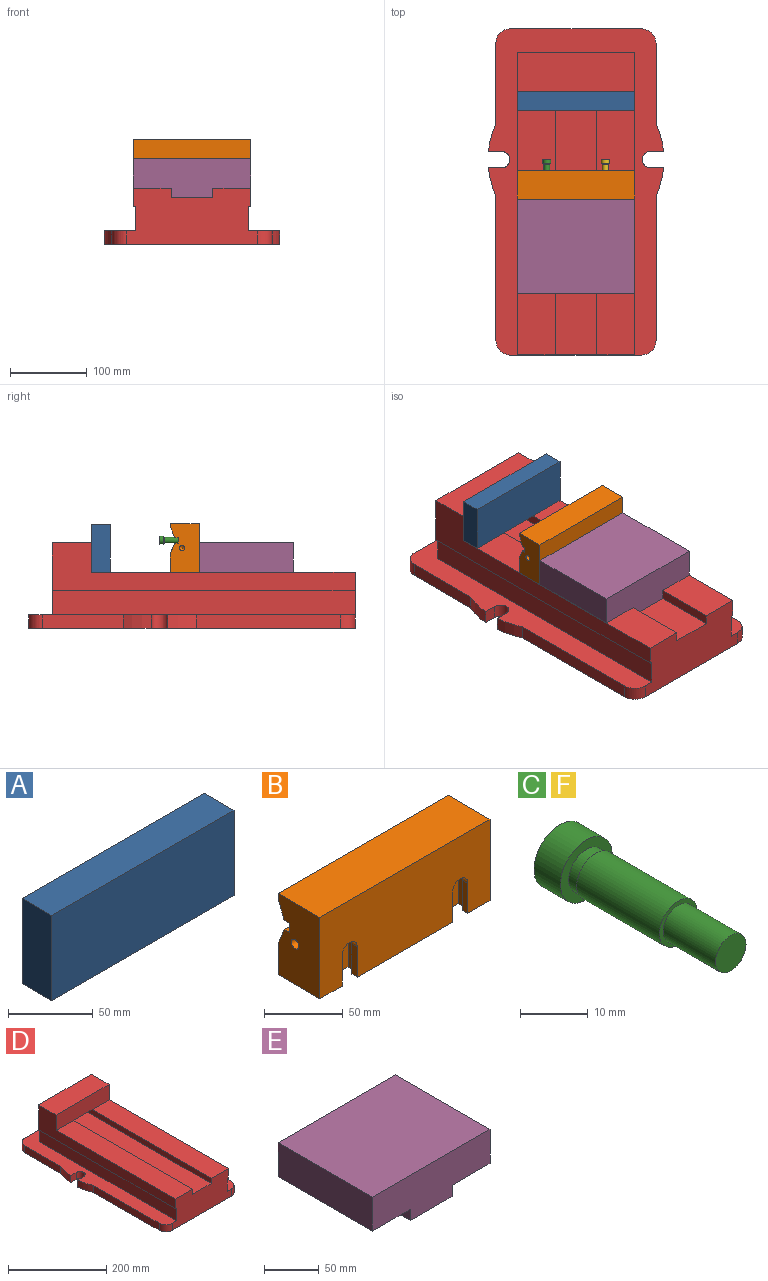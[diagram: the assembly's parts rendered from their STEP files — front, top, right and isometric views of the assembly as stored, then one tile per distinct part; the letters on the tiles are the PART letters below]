
ASSEMBLY  parts=6 mates=6
PART A: 6 faces, bbox 152.4x25x61.7 mm
  f0: plane 61.72x25.02mm, normal (-1,0,0), area 1544.2mm2, adj f1,f3,f4,f5
  f1: plane 152.4x25.02mm, normal (0,0,-1), area 3812.9mm2, adj f0,f2,f4,f5
  f2: plane 61.72x25.02mm, normal (1,0,0), area 1544.2mm2, adj f1,f3,f4,f5
  f3: plane 152.4x25.02mm, normal (0,0,1), area 3812.9mm2, adj f0,f2,f4,f5
  f4: plane 152.4x61.72mm, normal (0,-1,0), area 9406.4mm2, adj f0,f1,f2,f3
  f5: plane 152.4x61.72mm, normal (0,1,0), area 9406.4mm2, adj f0,f1,f2,f3
PART B: 56 faces, bbox 152.4x37.6x63 mm
  f0: plane 152.4x62.99mm, normal (0,-1,0), area 8811.2mm2, adj f2,f4,f12,f13,f42,f43,f47,f48
  f1: cylinder r=4.36mm len=25.65mm, axis (0,-1,0), area 688.4mm2, adj f5,f6,f40
  f2: plane 152.4x37.59mm, normal (0,0,-1), area 5300.4mm2, adj f0,f5,f12,f13,f40,f41,f42,f43
  f3: cylinder r=4.36mm len=25.65mm, axis (0,-1,0), area 688.4mm2, adj f5,f6,f46
  f4: plane 152.4x37.59mm, normal (0,0,1), area 5729mm2, adj f0,f11,f12,f13
  f5: plane 152.4x23.62mm, normal (0,1,0), area 3536mm2, adj f1,f2,f3,f6,f12,f13
  f6: plane 152.4x14.15mm, normal (0,0.93,0.37), area 2261.7mm2, adj f1,f3,f5,f7,f12,f13
  f7: plane 152.4x4.57mm, normal (0,0,1), area 696.8mm2, adj f6,f8,f12,f13
  f8: plane 152.4x7.14mm, normal (0,1,0), area 834.9mm2, adj f7,f9,f12,f13,f15,f17,f19,f21
  f9: plane 152.4x4.57mm, normal (0,0,-1), area 696.8mm2, adj f8,f10,f12,f13
  f10: plane 152.4x14.15mm, normal (0,0.93,-0.37), area 2321.1mm2, adj f9,f11,f12,f13
  f11: plane 152.4x3.94mm, normal (0,1,0), area 600mm2, adj f4,f10,f12,f13
  f12: plane 62.99x37.59mm, normal (1,0,0), area 2177.9mm2, adj f0,f2,f4,f5,f6,f7,f8,f9
  f13: plane 62.99x37.59mm, normal (-1,0,0), area 2177.9mm2, adj f0,f2,f4,f5,f6,f7,f8,f9
  f14: cone r=0mm half-angle=59deg, axis (0,1,0), area 26.8mm2, adj f15
  f15: cylinder r=2.71mm len=21.08mm, axis (0,1,0), area 358.3mm2, adj f8,f14
  f16: cone r=0mm half-angle=59deg, axis (0,1,0), area 26.8mm2, adj f17
  f17: cylinder r=2.71mm len=21.08mm, axis (0,1,0), area 358.3mm2, adj f8,f16
  f18: cone r=0mm half-angle=59deg, axis (0,1,0), area 26.8mm2, adj f19
  f19: cylinder r=2.71mm len=21.08mm, axis (0,1,0), area 358.3mm2, adj f8,f18
  f20: cone r=0mm half-angle=59deg, axis (0,1,0), area 26.8mm2, adj f21
  f21: cylinder r=2.71mm len=21.08mm, axis (0,1,0), area 358.3mm2, adj f8,f20
  f22: cone r=0mm half-angle=59deg, axis (0,1,0), area 26.8mm2, adj f23
  f23: cylinder r=2.71mm len=21.08mm, axis (0,1,0), area 358.3mm2, adj f8,f22
  f24: cone r=0mm half-angle=59deg, axis (0,1,0), area 26.8mm2, adj f25
  f25: cylinder r=2.71mm len=21.08mm, axis (0,1,0), area 358.3mm2, adj f8,f24
  f26: cone r=0mm half-angle=59deg, axis (0,1,0), area 26.8mm2, adj f27
  f27: cylinder r=2.71mm len=21.08mm, axis (0,1,0), area 358.3mm2, adj f8,f26
  f28: cone r=0mm half-angle=59deg, axis (0,1,0), area 26.8mm2, adj f29
  f29: cylinder r=2.71mm len=21.08mm, axis (0,1,0), area 358.3mm2, adj f8,f28
  f30: cone r=0mm half-angle=59deg, axis (0,1,0), area 26.8mm2, adj f31
  f31: cylinder r=2.71mm len=21.08mm, axis (0,1,0), area 358.3mm2, adj f8,f30
  f32: cone r=0mm half-angle=59deg, axis (0,1,0), area 26.8mm2, adj f33
  f33: cylinder r=2.71mm len=21.08mm, axis (0,1,0), area 358.3mm2, adj f8,f32
  f34: cone r=0mm half-angle=59deg, axis (0,1,0), area 26.8mm2, adj f35
  f35: cylinder r=2.71mm len=21.08mm, axis (0,1,0), area 358.3mm2, adj f8,f34
  f36: cone r=0mm half-angle=59deg, axis (1,0,0), area 43.7mm2, adj f37
  f37: cylinder r=3.45mm len=15.01mm, axis (1,0,0), area 325.8mm2, adj f12,f36
  f38: cone r=0mm half-angle=59deg, axis (-1,0,0), area 43.7mm2, adj f39
  f39: cylinder r=3.45mm len=15.01mm, axis (-1,0,0), area 325.8mm2, adj f13,f38
  f40: plane 33.78x20.83mm, normal (0,-1,0), area 597.5mm2, adj f1,f2,f44,f45,f53
  f41: plane 33.78x20.83mm, normal (0,1,0), area 262.7mm2, adj f2,f42,f43,f44,f45,f52,f53
  f42: plane 23.37x4.83mm, normal (-1,0,0), area 112.8mm2, adj f0,f2,f41,f52
  f43: plane 23.37x4.83mm, normal (1,0,0), area 112.8mm2, adj f0,f2,f41,f52
  f44: plane 23.37x7.11mm, normal (1,0,0), area 166.2mm2, adj f2,f40,f41,f53
  f45: plane 23.37x7.11mm, normal (-1,0,0), area 166.2mm2, adj f2,f40,f41,f53
  f46: plane 33.78x20.83mm, normal (0,-1,0), area 597.5mm2, adj f2,f3,f50,f51,f55
  f47: plane 23.37x4.83mm, normal (-1,0,0), area 112.8mm2, adj f0,f2,f49,f54
  f48: plane 23.37x4.83mm, normal (1,0,0), area 112.8mm2, adj f0,f2,f49,f54
  f49: plane 33.78x20.83mm, normal (0,1,0), area 262.7mm2, adj f2,f47,f48,f50,f51,f54,f55
  f50: plane 23.37x7.11mm, normal (1,0,0), area 166.2mm2, adj f2,f46,f49,f55
  f51: plane 23.37x7.11mm, normal (-1,0,0), area 166.2mm2, adj f2,f46,f49,f55
  f52: cylinder r=6.86mm len=13.72mm, axis (0,1,0), area 104mm2, adj f0,f41,f42,f43
  f53: cylinder r=10.41mm len=20.83mm, axis (0,1,0), area 232.7mm2, adj f40,f41,f44,f45
  f54: cylinder r=6.86mm len=13.72mm, axis (0,1,0), area 104mm2, adj f0,f47,f48,f49
  f55: cylinder r=10.41mm len=20.83mm, axis (0,1,0), area 232.7mm2, adj f46,f49,f50,f51
PART C: 16 faces, bbox 10.8x35.6x10.8 mm
  f0: plane 10.77x10.77mm, normal (0,1,0), area 75.9mm2, adj f1,f9,f10,f11,f12,f13,f14
  f1: cylinder r=5.38mm len=10.77mm, axis (0,1,0), area 186.5mm2, adj f0,f2
  f2: plane 10.77x10.77mm, normal (0,-1,0), area 48.5mm2, adj f1,f3
  f3: cylinder r=3.68mm len=7.37mm, axis (0,1,0), area 44.7mm2, adj f2,f4
  f4: plane 7.87x7.87mm, normal (0,1,0), area 6.1mm2, adj f3,f5
  f5: cylinder r=3.94mm len=17.2mm, axis (0,1,0), area 425.4mm2, adj f4,f6
  f6: plane 7.87x7.87mm, normal (0,-1,0), area 17mm2, adj f5,f7
  f7: cylinder r=3.17mm len=10.92mm, axis (0,1,0), area 217.9mm2, adj f6,f8
  f8: plane 6.35x6.35mm, normal (0,-1,0), area 31.7mm2, adj f7
  f9: plane 3.86x2.1mm, normal (-0.5,0,-0.87), area 9.3mm2, adj f0,f10,f14,f15
  f10: plane 3.86x2.42mm, normal (-1,0,0), area 9.3mm2, adj f0,f9,f11,f15
  f11: plane 3.86x2.1mm, normal (-0.5,0,0.87), area 9.3mm2, adj f0,f10,f12,f15
  f12: plane 3.86x2.1mm, normal (0.5,0,0.87), area 9.3mm2, adj f0,f11,f13,f15
  f13: plane 3.86x2.42mm, normal (1,0,0), area 9.3mm2, adj f0,f12,f14,f15
  f14: plane 3.86x2.1mm, normal (0.5,0,-0.87), area 9.3mm2, adj f0,f9,f13,f15
  f15: plane 4.84x4.19mm, normal (0,1,0), area 15.2mm2, adj f9,f10,f11,f12,f13,f14
PART D: 37 faces, bbox 227.6x423.9x111.1 mm
  f0: plane 187.5x17.46mm, normal (1,0,0), area 3274.3mm2, adj f1,f18,f19,f21
  f1: cylinder r=114.3mm len=36.77mm, axis (0,0,-1), area 667.7mm2, adj f0,f2,f18,f21
  f2: plane 17.46x16.96mm, normal (0,1,0), area 296.2mm2, adj f1,f3,f18,f21
  f3: cylinder r=10.67mm len=21.35mm, axis (0,0,-1), area 585.5mm2, adj f2,f4,f18,f21
  f4: plane 17.46x16.96mm, normal (0,-1,0), area 296.2mm2, adj f3,f5,f18,f21
  f5: cylinder r=114.3mm len=36.77mm, axis (0,0,-1), area 667.7mm2, adj f4,f6,f18,f21
  f6: plane 103.37x17.46mm, normal (1,0,0), area 1805mm2, adj f5,f7,f18,f21
  f7: cylinder r=19.05mm len=19.05mm, axis (0,0,-1), area 522.5mm2, adj f6,f8,f18,f21
  f8: plane 171.12x17.46mm, normal (0,1,0), area 2988.2mm2, adj f7,f9,f18,f21
  f9: cylinder r=17.81mm len=17.81mm, axis (0,0,-1), area 488.4mm2, adj f8,f10,f18,f21
  f10: plane 104.61x17.46mm, normal (-1,0,0), area 1826.8mm2, adj f9,f11,f18,f21
  f11: cylinder r=114.3mm len=36.77mm, axis (0,0,-1), area 667.7mm2, adj f10,f12,f18,f21
  f12: plane 17.46x16.96mm, normal (0,-1,0), area 296.2mm2, adj f11,f13,f18,f21
  f13: cylinder r=10.67mm len=21.35mm, axis (0,0,-1), area 585.5mm2, adj f12,f14,f18,f21
  f14: plane 17.46x16.96mm, normal (0,1,0), area 296.2mm2, adj f13,f15,f18,f21
  f15: cylinder r=114.3mm len=36.77mm, axis (0,0,-1), area 667.7mm2, adj f14,f16,f18,f21
  f16: plane 187.5x17.46mm, normal (-1,0,0), area 3274.3mm2, adj f15,f17,f18,f21
  f17: cylinder r=19.05mm len=19.05mm, axis (0,0,-1), area 522.5mm2, adj f16,f18,f21,f27
  f18: plane 423.86x227.6mm, normal (0,0,-1), area 88071.8mm2, adj f0,f1,f2,f3,f4,f5,f6,f7
  f19: cylinder r=19.05mm len=19.05mm, axis (0,0,-1), area 522.5mm2, adj f0,f18,f21,f27
  f20: plane 393.7x31.75mm, normal (1,0,0), area 12500mm2, adj f21,f27,f28,f29
  f21: plane 423.86x227.6mm, normal (0,0,1), area 30572mm2, adj f0,f1,f2,f3,f4,f5,f6,f7
  f22: plane 393.7x31.75mm, normal (-1,0,0), area 12500mm2, adj f21,f24,f27,f29
  f23: plane 393.7x53.98mm, normal (0,0,1), area 21250mm2, adj f25,f26,f27,f29
  f24: plane 393.7x3.18mm, normal (0,0,-1), area 1250mm2, adj f22,f27,f29,f31
  f25: plane 393.7x12.7mm, normal (1,0,0), area 5000mm2, adj f23,f27,f29,f32,f33
  f26: plane 393.7x12.7mm, normal (-1,0,0), area 5000mm2, adj f23,f27,f29,f33,f34
  f27: plane 169.88x73.03mm, normal (0,-1,0), area 10547.1mm2, adj f17,f18,f19,f20,f21,f22,f23,f24
  f28: plane 393.7x3.18mm, normal (0,0,-1), area 1250mm2, adj f20,f27,f29,f35
  f29: plane 152.4x93.66mm, normal (0,1,0), area 13387.1mm2, adj f20,f21,f22,f23,f24,f25,f26,f28
  f30: plane 152.4x50.8mm, normal (0,0,1), area 7741.9mm2, adj f29,f31,f35,f36
  f31: plane 393.7x61.91mm, normal (-1,0,0), area 11310.5mm2, adj f24,f27,f29,f30,f32,f36
  f32: plane 342.9x49.21mm, normal (0,0,1), area 16875mm2, adj f25,f27,f31,f36
  f33: plane 53.98x50.8mm, normal (0,0,-1), area 2741.9mm2, adj f25,f26,f29,f36
  f34: plane 342.9x49.21mm, normal (0,0,1), area 16875mm2, adj f26,f27,f35,f36
  f35: plane 393.7x61.91mm, normal (1,0,0), area 11310.5mm2, adj f27,f28,f29,f30,f34,f36
  f36: plane 152.4x38.1mm, normal (0,-1,0), area 5806.4mm2, adj f30,f31,f32,f33,f34,f35
PART E: 10 faces, bbox 152.4x122.2x50.8 mm
  f0: plane 152.4x122.24mm, normal (0,0,1), area 18629mm2, adj f1,f4,f6,f8
  f1: plane 122.24x38.1mm, normal (1,0,0), area 4657.2mm2, adj f0,f2,f6,f8
  f2: plane 122.24x49.21mm, normal (0,0,-1), area 6015.6mm2, adj f1,f3,f6,f8
  f3: plane 122.24x12.7mm, normal (1,0,0), area 1552.4mm2, adj f2,f5,f6,f8
  f4: plane 122.24x38.1mm, normal (-1,0,0), area 4657.2mm2, adj f0,f6,f7,f8
  f5: plane 122.24x53.98mm, normal (0,0,-1), area 6597.8mm2, adj f3,f6,f8,f9
  f6: plane 152.4x50.8mm, normal (0,-1,0), area 6491.9mm2, adj f0,f1,f2,f3,f4,f5,f7,f9
  f7: plane 122.24x49.21mm, normal (0,0,-1), area 6015.6mm2, adj f4,f6,f8,f9
  f8: plane 152.4x50.8mm, normal (0,1,0), area 6491.9mm2, adj f0,f1,f2,f3,f4,f5,f7,f9
  f9: plane 122.24x12.7mm, normal (-1,0,0), area 1552.4mm2, adj f5,f6,f7,f8
PART F: same geometry as C
PLACE A t=(-76.2,0,0)mm
PLACE B t=(0,-140.44,0)mm
PLACE C t=(-38.1,-123.98,41.33)mm
PLACE D t=(0,-146.05,-23.81)mm
PLACE E t=(0,-140.44,0)mm
PLACE F t=(38.1,-123.98,41.33)mm
MATE fastened D.f33 <-> A.f1  axis (0,0,1) through (0,0,0)mm
MATE fastened E.f2 <-> B.f2  axis (0,0,1) through (0,-140.44,0)mm
MATE fastened B.f18 <-> F.f1  axis (0,1,0) through (38.1,-113.06,41.33)mm
MATE planar D.f35 <-> E.f1  axis (1,0,0) through (76.2,-171.45,0)mm
MATE planar E.f2 <-> D.f34  axis (0,0,-1) through (51.59,-201.56,0)mm
MATE fastened B.f30 <-> C.f1  axis (0,1,0) through (-38.1,-113.06,41.33)mm
